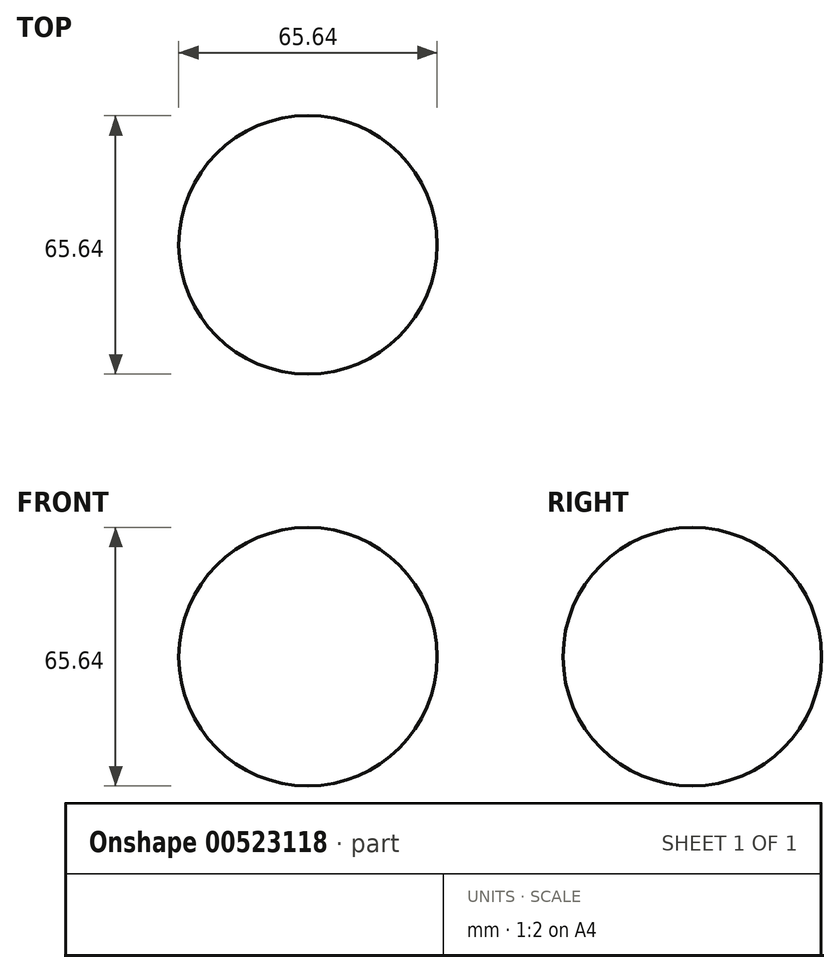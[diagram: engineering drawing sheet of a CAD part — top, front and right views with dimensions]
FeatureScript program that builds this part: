
annotation { "Feature Type Name" : "Feature", "Feature Type Description" : "" }
export const myFeature = defineFeature(function(context is Context, id is Id, definition is map)
    precondition{}
    {
        {
            var Q0;
            Q0=qCreatedBy(makeId("Front.planeOp"),FACE);
            var sketch = newSketch(context, id + "F0", { "sketchPlane" : qUnion([Q0])});
            skCircle(sketch, "E0", {"center": v(0, 0) * mm, "radius": 32.82 * mm});
            skLineSegment(sketch, "E1", {"start": v(0, -32.82) * mm, "end": v(0, 32.82) * mm});
            skSolve(sketch);
        }
        {
            var Q0;
            {var subQ0=sQuery(id+"F0.wireOp",EDGE,"E1");Q0=makeQuery(id+"F0.imprint","IMPRINT",FACE,{"disambiguationData":[TD([[makeQuery(id+"F0.imprint","IMPRINT",EDGE,{"derivedFrom":subQ0}),1.0]])]});}
            var Q1;
            Q1=sQuery(id+"F0.wireOp",EDGE,"E1");
            revolve(context, id + "F1", {"entities" : qUnion([Q0]), "axis" : qUnion([Q1]), "revolveType" : RevolveType.FULL});
        }
    });
